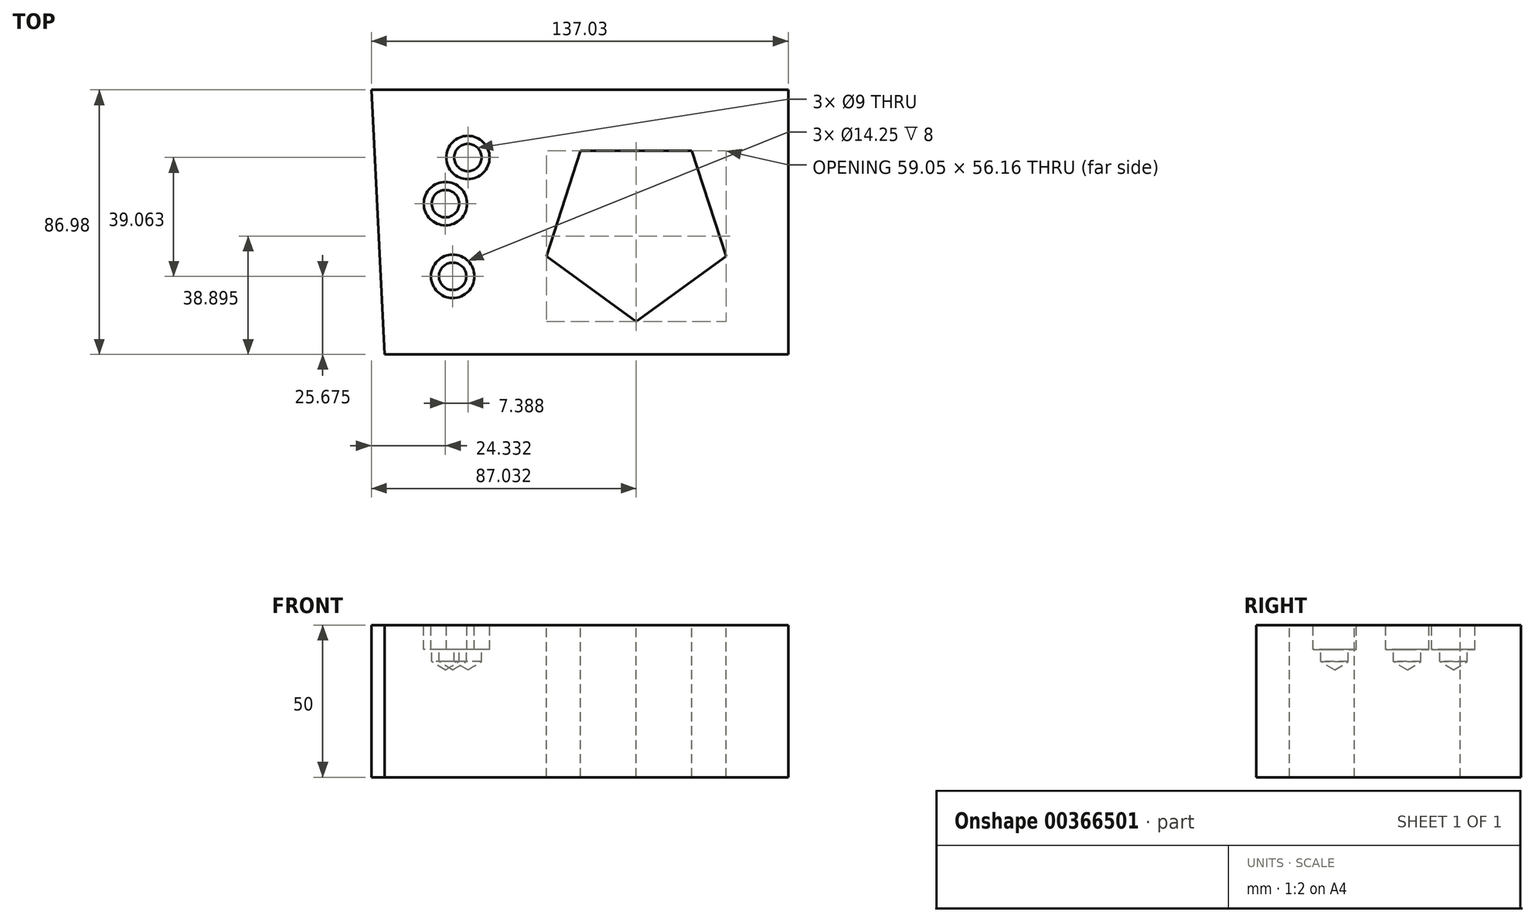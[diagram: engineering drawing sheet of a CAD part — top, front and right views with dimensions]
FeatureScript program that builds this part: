
annotation { "Feature Type Name" : "Feature", "Feature Type Description" : "" }
export const myFeature = defineFeature(function(context is Context, id is Id, definition is map)
    precondition{}
    {
        {
            var Q0;
            Q0=qCreatedBy(makeId("Top.planeOp"),FACE);
            var sketch = newSketch(context, id + "F0", { "sketchPlane" : qUnion([Q0])});
            skLineSegment(sketch, "E0", {"start": v(-104.82, -41.86) * mm, "end": v(-109.12, 45.12) * mm});
            skLineSegment(sketch, "E1", {"start": v(-109.12, 45.12) * mm, "end": v(27.91, 45.12) * mm});
            skLineSegment(sketch, "E2", {"start": v(27.91, 45.12) * mm, "end": v(27.91, -41.86) * mm});
            skLineSegment(sketch, "E3", {"start": v(27.91, -41.86) * mm, "end": v(-104.82, -41.86) * mm});
            skSolve(sketch);
        }
        {
            var Q0;
            Q0=makeQuery(id+"F0.imprint","IMPRINT",FACE,{"disambiguationData":[TD([[makeQuery(id+"F0.imprint","IMPRINT",EDGE,{"derivedFrom":sQuery(id+"F0.wireOp",EDGE,"E0")}),-1.0]])]});
            extrude(context, id + "F1", {"entities" : qUnion([Q0]), "depth" : 101.6 * mm});
        }
        {
            var Q0;
            Q0=makeQuery(id+"F1.opExtrude","SWEPT_FACE",FACE,{"disambiguationData":[OSD([sQuery(id+"F0.wireOp",EDGE,"E3")])]});
            var sketch = newSketch(context, id + "F2", { "sketchPlane" : qUnion([Q0])});
            skLineSegment(sketch, "E4", {"start": v(-104.82, 50.8) * mm, "end": v(-134.82, 50.8) * mm});
            skLineSegment(sketch, "E5", {"start": v(-134.82, 50.8) * mm, "end": v(-107.76, 0) * mm});
            skLineSegment(sketch, "E6", {"start": v(-107.76, 0) * mm, "end": v(-104.82, 0) * mm});
            skSolve(sketch);
        }
        {
            var Q0;
            Q0 = qSketchRegion(id + "F2", true);
            var Q1;
            {var subQ0=sQuery(id+"F2.wireOp",EDGE,"E4");Q1=makeQuery(id+"F2.imprint","IMPRINT",FACE,{"disambiguationData":[TD([[makeQuery(id+"F2.imprint","IMPRINT",EDGE,{"derivedFrom":subQ0}),1.0]])]});}
            var Q2;
            Q2=makeQuery(id+"F1.opExtrude","SWEPT_EDGE",EDGE,{"disambiguationData":[OSD([sQuery(id+"F0.wireOp",EDGE,"E2"),sQuery(id+"F0.wireOp",EDGE,"E3")])]});
            revolve(context, id + "F3", {"operationType" : NewBodyOperationType.ADD, "entities" : qUnion([Q0, Q1]), "axis" : qUnion([Q2]), "revolveType" : RevolveType.FULL});
        }
        {
            var Q0;
            Q0=makeQuery(id+"F1.opExtrude","CAP_FACE",FACE,{"disambiguationData":[OSD([sQuery(id+"F0.wireOp",EDGE,"E0"),sQuery(id+"F0.wireOp",EDGE,"E1"),sQuery(id+"F0.wireOp",EDGE,"E2"),sQuery(id+"F0.wireOp",EDGE,"E3")])],"isStart":false});
            var sketch = newSketch(context, id + "F4", { "sketchPlane" : qUnion([Q0])});
            skCircle(sketch, "E7.cCircle", {"center": v(-22.09, 0) * mm, "radius": 25.12 * mm, "construction": true});
            skLineSegment(sketch, "E7.0", {"start": v(-40.34, 25.12) * mm, "end": v(-3.84, 25.12) * mm});
            skLineSegment(sketch, "E7.1", {"start": v(-3.84, 25.12) * mm, "end": v(7.44, -9.6) * mm});
            skLineSegment(sketch, "E7.2", {"start": v(7.44, -9.6) * mm, "end": v(-22.09, -31.05) * mm});
            skLineSegment(sketch, "E7.3", {"start": v(-22.09, -31.05) * mm, "end": v(-51.61, -9.6) * mm});
            skLineSegment(sketch, "E7.4", {"start": v(-51.61, -9.6) * mm, "end": v(-40.34, 25.12) * mm});
            skPoint(sketch, "E7.0.midPoint", {"position": v(-22.09, 25.12) * mm});
            skSolve(sketch);
        }
        {
            var Q0;
            Q0=makeQuery(id+"F4.imprint","IMPRINT",FACE,{"disambiguationData":[TD([[makeQuery(id+"F4.imprint","IMPRINT",EDGE,{"derivedFrom":sQuery(id+"F4.wireOp",EDGE,"E7.0")}),1.0]])]});
            extrude(context, id + "F5", {"entities" : qUnion([Q0]), "operationType" : NewBodyOperationType.INTERSECT, "oppositeDirection" : true, "depth" : 50 * mm, "offsetDistance" : 25 * mm});
        }
        {
            var Q0;
            Q0=makeQuery(id+"F1.opExtrude","CAP_FACE",FACE,{"disambiguationData":[OSD([sQuery(id+"F0.wireOp",EDGE,"E0"),sQuery(id+"F0.wireOp",EDGE,"E1"),sQuery(id+"F0.wireOp",EDGE,"E2"),sQuery(id+"F0.wireOp",EDGE,"E3")])],"isStart":false});
            var sketch = newSketch(context, id + "F6", { "sketchPlane" : qUnion([Q0])});
            skPoint(sketch, "E8", {"position": v(-84.79, 7.7) * mm});
            skPoint(sketch, "E9", {"position": v(-82.4, -16.19) * mm});
            skPoint(sketch, "E10", {"position": v(-77.4, 22.88) * mm});
            skSolve(sketch);
        }
        {
            var Q0;
            Q0=sQuery(id+"F6.wireOp",VERTEX,"E9");
            var Q1;
            Q1=sQuery(id+"F6.wireOp",VERTEX,"E8");
            var Q2;
            Q2=sQuery(id+"F6.wireOp",VERTEX,"E10");
            var Q3;
            Q3=makeQuery(id+"F1.opExtrude","SWEPT_BODY",BODY,{"disambiguationData":[OSD([sQuery(id+"F0.wireOp",EDGE,"E0"),sQuery(id+"F0.wireOp",EDGE,"E1"),sQuery(id+"F0.wireOp",EDGE,"E2"),sQuery(id+"F0.wireOp",EDGE,"E3")])]});
            hole(context, id + "F7", {"style" : HoleStyle.C_BORE, "endStyle" : HoleEndStyle.BLIND, "standardTappedOrClearance" : lookupTablePath({ "fit" : "Normal", "standard" : "ISO", "size" : "M8", "type" : "Clearance" }), "standardBlindInLast" : lookupTablePath({ "fit" : "Normal", "standard" : "ISO", "engagement" : "75%", "pitch" : "1.25 mm", "size" : "M8", "type" : "Clearance & tapped" }), "holeDiameter" : 9 * mm, "cBoreDiameter" : 14.25 * mm, "cBoreDepth" : 8 * mm, "majorDiameter" : 5 * mm, "holeDepth" : 12 * mm, "isTappedThrough" : true, "tappedDepth" : 12 * mm, "tapClearance" : 3, "locations" : qUnion([Q0, Q1, Q2]), "scope" : qUnion([Q3])});
        }
    });
